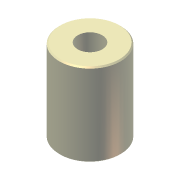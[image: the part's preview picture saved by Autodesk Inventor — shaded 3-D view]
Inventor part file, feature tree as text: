
AUTODESK INVENTOR PART (.ipt)
format: ipt  version: 2011 (Build 150239000, 239)  size: 87,552 bytes
history: native  units: in
note: dims shown in document units (in); Inventor stores cm internally (conversion verified against a paired STEP export)
features: chamfer x1, imported_body x1
ambient origin geometry x8: Origin, YZ Plane, XZ Plane, XY Plane, X Axis, Y Axis, Z Axis, Center Point
feature tree (2):
  chamfer  "Chamfer1"  [1 undecoded]
  imported_body  "Base1"
note: 1 required parameter value undecoded (feature->parameter linkage not recoverable at this tier; creation-order binding heuristic only, values carry confidence <= 0.55)
